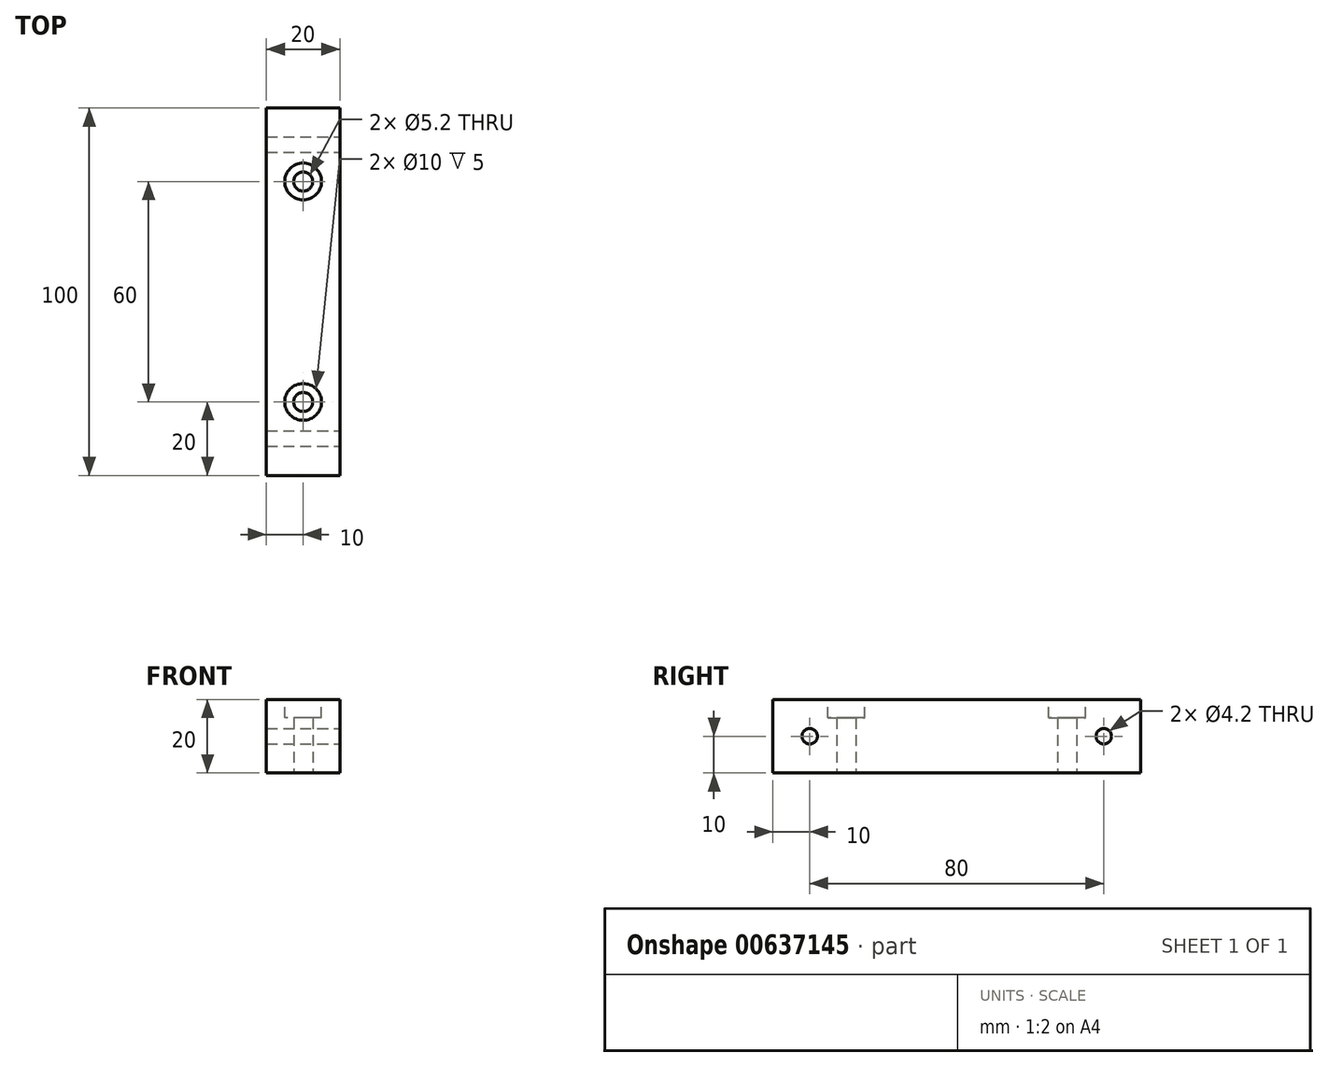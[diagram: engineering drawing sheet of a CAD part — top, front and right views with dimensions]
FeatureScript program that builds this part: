
annotation { "Feature Type Name" : "Feature", "Feature Type Description" : "" }
export const myFeature = defineFeature(function(context is Context, id is Id, definition is map)
    precondition{}
    {
        {
            var Q0;
            Q0=qCreatedBy(makeId("Top.planeOp"),FACE);
            var sketch = newSketch(context, id + "F0", { "sketchPlane" : qUnion([Q0])});
            skLineSegment(sketch, "E0.bottom", {"start": v(10, -50) * mm, "end": v(-10, -50) * mm});
            skLineSegment(sketch, "E0.top", {"start": v(10, 50) * mm, "end": v(-10, 50) * mm});
            skLineSegment(sketch, "E0.left", {"start": v(10, -50) * mm, "end": v(10, 50) * mm});
            skLineSegment(sketch, "E0.right", {"start": v(-10, -50) * mm, "end": v(-10, 50) * mm});
            skPoint(sketch, "E0.middle", {"position": v(0, 0) * mm});
            skLineSegment(sketch, "E1", {"start": v(0, 50) * mm, "end": v(0, -50) * mm, "construction": true});
            skCircle(sketch, "E2", {"center": v(0, 30) * mm, "radius": 2.6 * mm});
            skCircle(sketch, "E3", {"center": v(0, -30) * mm, "radius": 2.6 * mm});
            skSolve(sketch);
        }
        {
            var Q0;
            Q0=makeQuery(id+"F0.imprint","IMPRINT",FACE,{"disambiguationData":[TD([[makeQuery(id+"F0.imprint","IMPRINT",EDGE,{"derivedFrom":sQuery(id+"F0.wireOp",EDGE,"E0.bottom")}),-1.0]])]});
            extrude(context, id + "F1", {"entities" : qUnion([Q0]), "depth" : 20 * mm, "offsetDistance" : 25 * mm});
        }
        {
            var Q0;
            Q0=makeQuery(id+"F1.opExtrude","CAP_FACE",FACE,{"disambiguationData":[OSD([sQuery(id+"F0.wireOp",EDGE,"E0.bottom"),sQuery(id+"F0.wireOp",EDGE,"E0.top"),sQuery(id+"F0.wireOp",EDGE,"E0.left"),sQuery(id+"F0.wireOp",EDGE,"E0.right"),sQuery(id+"F0.wireOp",EDGE,"E2"),sQuery(id+"F0.wireOp",EDGE,"E3")])],"isStart":false});
            var sketch = newSketch(context, id + "F2", { "sketchPlane" : qUnion([Q0])});
            skCircle(sketch, "E4", {"center": v(0, 30) * mm, "radius": 5 * mm});
            skCircle(sketch, "E5", {"center": v(0, -30) * mm, "radius": 5 * mm});
            skSolve(sketch);
        }
        {
            var Q0;
            Q0 = qSketchRegion(id + "F2", true);
            extrude(context, id + "F3", {"entities" : qUnion([Q0]), "operationType" : NewBodyOperationType.REMOVE, "oppositeDirection" : true, "depth" : 5 * mm, "offsetDistance" : 25 * mm});
        }
        {
            var Q0;
            Q0=makeQuery(id+"F1.opExtrude","SWEPT_FACE",FACE,{"disambiguationData":[OSD([sQuery(id+"F0.wireOp",EDGE,"E0.left")])]});
            var sketch = newSketch(context, id + "F4", { "sketchPlane" : qUnion([Q0])});
            skLineSegment(sketch, "E6", {"start": v(-50, 10) * mm, "end": v(50, 10) * mm, "construction": true});
            skCircle(sketch, "E7", {"center": v(-40, 10) * mm, "radius": 2.1 * mm});
            skCircle(sketch, "E8", {"center": v(40, 10) * mm, "radius": 2.1 * mm});
            skSolve(sketch);
        }
        {
            var Q0;
            Q0=makeQuery(id+"F4.imprint","IMPRINT",FACE,{"disambiguationData":[TD([[makeQuery(id+"F4.imprint","IMPRINT",EDGE,{"derivedFrom":sQuery(id+"F4.wireOp",EDGE,"E7")}),1.0]])]});
            var Q1;
            Q1=makeQuery(id+"F4.imprint","IMPRINT",FACE,{"disambiguationData":[TD([[makeQuery(id+"F4.imprint","IMPRINT",EDGE,{"derivedFrom":sQuery(id+"F4.wireOp",EDGE,"E8")}),1.0]])]});
            extrude(context, id + "F5", {"entities" : qUnion([Q0, Q1]), "operationType" : NewBodyOperationType.REMOVE, "oppositeDirection" : true, "depth" : 25 * mm, "offsetDistance" : 25 * mm});
        }
    });
